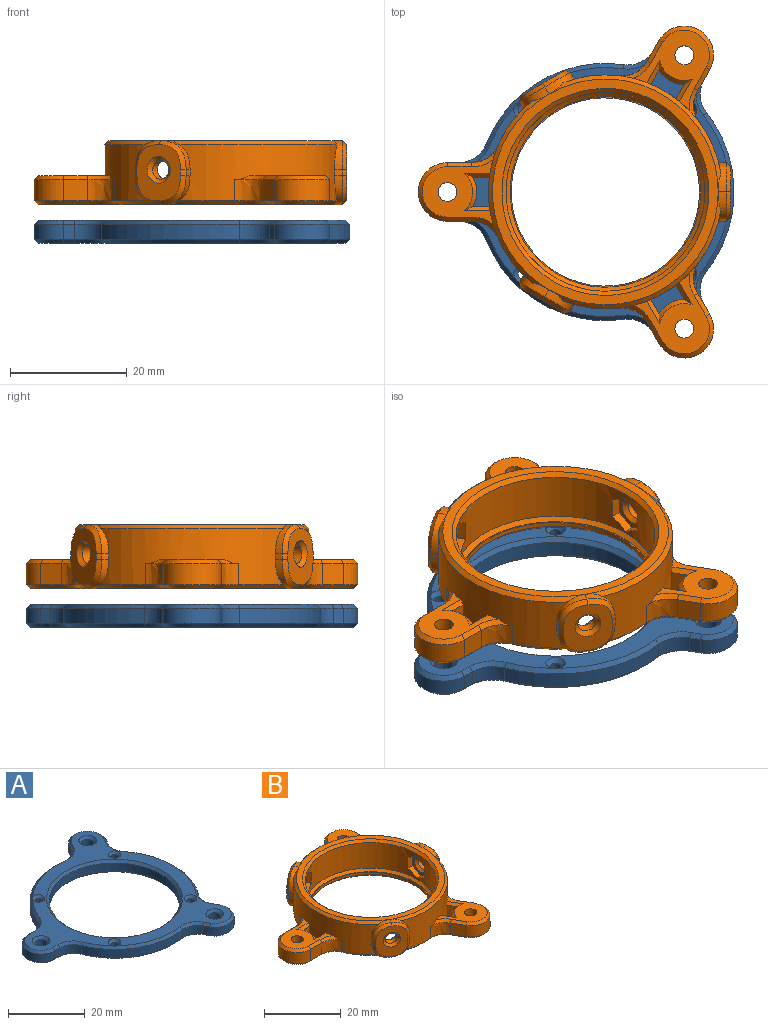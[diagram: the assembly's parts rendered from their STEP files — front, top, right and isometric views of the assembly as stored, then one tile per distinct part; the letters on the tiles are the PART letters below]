
ASSEMBLY  parts=2 mates=1
PART A: 79 faces, bbox 54x56.8x4 mm
  f0: plane 2.6x1.66mm, normal (-0.87,-0.5,0), area 5mm2, adj f1,f22,f44,f64
  f1: cylinder r=5mm len=9.33mm, axis (0,0,-1), area 40.8mm2, adj f0,f2,f46,f66
  f2: plane 2.6x1.66mm, normal (0.87,0.5,0), area 5mm2, adj f1,f23,f45,f65
  f3: cylinder r=22mm len=27.25mm, axis (0,0,-1), area 76.4mm2, adj f23,f24,f41,f61
  f4: plane 2.6x1.66mm, normal (0.87,-0.5,0), area 5mm2, adj f5,f24,f37,f56
  f5: cylinder r=5mm len=9.33mm, axis (0,0,-1), area 40.8mm2, adj f4,f6,f35,f54
  f6: plane 2.6x1.66mm, normal (-0.87,0.5,0), area 5mm2, adj f5,f25,f33,f52
  f7: cylinder r=22mm len=23.6mm, axis (0,0,-1), area 76.4mm2, adj f25,f26,f29,f48
  f8: plane 2.6x1.92mm, normal (0,1,0), area 5mm2, adj f9,f26,f32,f51
  f9: cylinder r=5mm len=10mm, axis (0,0,-1), area 40.8mm2, adj f8,f10,f34,f53
  f10: plane 2.6x1.92mm, normal (0,-1,0), area 5mm2, adj f9,f27,f36,f55
  f11: cylinder r=1.6mm len=3.2mm, axis (0,0,-1), area 26.1mm2, adj f71,f72
  f12: cylinder r=0.95mm len=3.3mm, axis (0,0,-1), area 19.7mm2, adj f21,f58
  f13: cylinder r=0.95mm len=2.6mm, axis (0,0,-1), area 15.5mm2, adj f28,f47
  f14: cylinder r=0.95mm len=2.6mm, axis (0,0,-1), area 15.5mm2, adj f68,f75
  f15: cylinder r=0.95mm len=2.6mm, axis (0,0,-1), area 15.5mm2, adj f69,f74
  f16: cylinder r=17mm len=34mm, axis (0,0,-1), area 277.7mm2, adj f77,f78
  f17: cylinder r=1.6mm len=3.2mm, axis (0,0,-1), area 26.1mm2, adj f70,f73
  f18: cylinder r=22mm len=23.6mm, axis (0,0,-1), area 76.4mm2, adj f22,f27,f40,f60
  f19: cylinder r=1.6mm len=3.2mm, axis (0,0,-1), area 26.1mm2, adj f67,f76
  f20: plane 55.37x52.6mm, normal (0,0,1), area 613.8mm2, adj f47,f48,f49,f50,f51,f52,f53,f54
  f21: plane 55.37x52.6mm, normal (0,0,-1), area 619.4mm2, adj f12,f28,f29,f30,f31,f32,f33,f34
  f22: cylinder r=5mm len=5.05mm, axis (0,0,-1), area 15.5mm2, adj f0,f18,f42,f62
  f23: cylinder r=5mm len=5.6mm, axis (0,0,-1), area 15.5mm2, adj f2,f3,f43,f63
  f24: cylinder r=5mm len=5.6mm, axis (0,0,-1), area 15.5mm2, adj f3,f4,f39,f59
  f25: cylinder r=5mm len=5.05mm, axis (0,0,-1), area 15.5mm2, adj f6,f7,f31,f50
  f26: cylinder r=5mm len=4.64mm, axis (0,0,-1), area 15.5mm2, adj f7,f8,f30,f49
  f27: cylinder r=5mm len=4.64mm, axis (0,0,-1), area 15.5mm2, adj f10,f18,f38,f57
  f28: cone r=1.65mm half-angle=45deg, axis (0,0,-1), area 8mm2, adj f13,f21,f29
  f29: cone r=22mm half-angle=45deg, axis (0,0,1), area 28.5mm2, adj f7,f21,f28,f30,f31
  f30: cone r=5.7mm half-angle=45deg, axis (0,0,-1), area 6.3mm2, adj f21,f26,f29,f32
  f31: cone r=5.7mm half-angle=45deg, axis (0,0,-1), area 6.3mm2, adj f21,f25,f29,f33
  f32: plane 1.92x0.7mm, normal (0,0.71,-0.71), area 1.9mm2, adj f8,f21,f30,f34
  f33: plane 2.01x1.57mm, normal (-0.61,0.35,-0.71), area 1.9mm2, adj f6,f21,f31,f35
  f34: cone r=5mm half-angle=45deg, axis (0,0,1), area 14.5mm2, adj f9,f21,f32,f36
  f35: cone r=5mm half-angle=45deg, axis (0,0,1), area 14.5mm2, adj f5,f21,f33,f37
  f36: plane 1.92x0.7mm, normal (0,-0.71,-0.71), area 1.9mm2, adj f10,f21,f34,f38
  f37: plane 2.01x1.57mm, normal (0.61,-0.35,-0.71), area 1.9mm2, adj f4,f21,f35,f39
  f38: cone r=5.7mm half-angle=45deg, axis (0,0,-1), area 6.3mm2, adj f21,f27,f36,f40
  f39: cone r=5.7mm half-angle=45deg, axis (0,0,-1), area 6.3mm2, adj f21,f24,f37,f41
  f40: cone r=22mm half-angle=45deg, axis (0,0,1), area 28.6mm2, adj f18,f21,f38,f42
  f41: cone r=22mm half-angle=45deg, axis (0,0,1), area 28.6mm2, adj f3,f21,f39,f43
  f42: cone r=5.7mm half-angle=45deg, axis (0,0,-1), area 6.3mm2, adj f21,f22,f40,f44
  f43: cone r=5.7mm half-angle=45deg, axis (0,0,-1), area 6.3mm2, adj f21,f23,f41,f45
  f44: plane 2.01x1.57mm, normal (-0.61,-0.35,-0.71), area 1.9mm2, adj f0,f21,f42,f46
  f45: plane 2.01x1.57mm, normal (0.61,0.35,-0.71), area 1.9mm2, adj f2,f21,f43,f46
  f46: cone r=5mm half-angle=45deg, axis (0,0,1), area 14.5mm2, adj f1,f21,f44,f45
  f47: cone r=0.95mm half-angle=45deg, axis (0,0,1), area 8mm2, adj f13,f20,f48
  f48: cone r=21.3mm half-angle=45deg, axis (0,0,-1), area 28.5mm2, adj f7,f20,f47,f49,f50
  f49: cone r=5.7mm half-angle=45deg, axis (0,0,1), area 6.3mm2, adj f20,f26,f48,f51
  f50: cone r=5.7mm half-angle=45deg, axis (0,0,1), area 6.3mm2, adj f20,f25,f48,f52
  f51: plane 1.92x0.7mm, normal (0,0.71,0.71), area 1.9mm2, adj f8,f20,f49,f53
  f52: plane 2.01x1.57mm, normal (-0.61,0.35,0.71), area 1.9mm2, adj f6,f20,f50,f54
  f53: cone r=4.3mm half-angle=45deg, axis (0,0,-1), area 14.5mm2, adj f9,f20,f51,f55
  f54: cone r=4.3mm half-angle=45deg, axis (0,0,-1), area 14.5mm2, adj f5,f20,f52,f56
  f55: plane 1.92x0.7mm, normal (0,-0.71,0.71), area 1.9mm2, adj f10,f20,f53,f57
  f56: plane 2.01x1.57mm, normal (0.61,-0.35,0.71), area 1.9mm2, adj f4,f20,f54,f59
  f57: cone r=5.7mm half-angle=45deg, axis (0,0,1), area 6.3mm2, adj f20,f27,f55,f60
  f58: cone r=0.95mm half-angle=45deg, axis (0,0,1), area 8mm2, adj f12,f20,f60
  f59: cone r=5.7mm half-angle=45deg, axis (0,0,1), area 6.3mm2, adj f20,f24,f56,f61
  f60: cone r=21.3mm half-angle=45deg, axis (0,0,-1), area 28.5mm2, adj f18,f20,f57,f58,f62
  f61: cone r=21.3mm half-angle=45deg, axis (0,0,-1), area 28.6mm2, adj f3,f20,f59,f63
  f62: cone r=5.7mm half-angle=45deg, axis (0,0,1), area 6.3mm2, adj f20,f22,f60,f64
  f63: cone r=5.7mm half-angle=45deg, axis (0,0,1), area 6.3mm2, adj f20,f23,f61,f65
  f64: plane 2.01x1.57mm, normal (-0.61,-0.35,0.71), area 1.9mm2, adj f0,f20,f62,f66
  f65: plane 2.01x1.57mm, normal (0.61,0.35,0.71), area 1.9mm2, adj f2,f20,f63,f66
  f66: cone r=4.3mm half-angle=45deg, axis (0,0,-1), area 14.5mm2, adj f1,f20,f64,f65
  f67: cone r=2.3mm half-angle=45deg, axis (0,0,-1), area 12.1mm2, adj f19,f21
  f68: cone r=1.65mm half-angle=45deg, axis (0,0,-1), area 8.1mm2, adj f14,f21
  f69: cone r=1.65mm half-angle=45deg, axis (0,0,-1), area 8.1mm2, adj f15,f21
  f70: cone r=2.3mm half-angle=45deg, axis (0,0,-1), area 12.1mm2, adj f17,f21
  f71: cone r=2.3mm half-angle=45deg, axis (0,0,-1), area 12.1mm2, adj f11,f21
  f72: cone r=1.6mm half-angle=45deg, axis (0,0,1), area 12.1mm2, adj f11,f20
  f73: cone r=1.6mm half-angle=45deg, axis (0,0,1), area 12.1mm2, adj f17,f20
  f74: cone r=0.95mm half-angle=45deg, axis (0,0,1), area 8.1mm2, adj f15,f20
  f75: cone r=0.95mm half-angle=45deg, axis (0,0,1), area 8.1mm2, adj f14,f20
  f76: cone r=1.6mm half-angle=45deg, axis (0,0,1), area 12.1mm2, adj f19,f20
  f77: cone r=17.7mm half-angle=45deg, axis (0,0,-1), area 107.9mm2, adj f16,f21
  f78: cone r=17mm half-angle=45deg, axis (0,0,1), area 107.9mm2, adj f16,f20
PART B: 173 faces, bbox 53.9x57.2x11.6 mm
  f0: cylinder r=17mm len=34mm, axis (0,0,-1), area 771.2mm2, adj f41,f42,f43,f44,f45,f46,f47,f48
  f1: plane 10x7.85mm, normal (-0.5,-0.87,0), area 54.1mm2, adj f104,f105,f106,f107,f108,f109,f149
  f2: plane 10x7.84mm, normal (-0.5,0.87,0), area 54.1mm2, adj f116,f117,f118,f119,f120,f121,f151
  f3: plane 10x9mm, normal (1,0,0), area 54.1mm2, adj f110,f111,f112,f113,f114,f115,f150
  f4: cylinder r=20mm len=27.02mm, axis (0,0,-1), area 267.1mm2, adj f9,f10,f34,f36,f38,f65,f66,f71
  f5: cylinder r=20mm len=31.2mm, axis (0,0,-1), area 267.1mm2, adj f7,f8,f24,f29,f30,f69,f70,f72
  f6: cylinder r=20mm len=27.02mm, axis (0,0,-1), area 267.1mm2, adj f11,f12,f15,f17,f22,f67,f68,f75
  f7: plane 1.18x1mm, normal (-0.87,-0.5,0), area 1.4mm2, adj f5,f79,f81,f119
  f8: plane 1.18x1mm, normal (-0.87,0.5,0), area 1.4mm2, adj f5,f72,f74,f105
  f9: plane 1.18x1mm, normal (0.87,-0.5,0), area 1.4mm2, adj f4,f71,f73,f108
  f10: plane 1.36x1mm, normal (0,-1,0), area 1.4mm2, adj f4,f76,f78,f111
  f11: plane 1.36x1mm, normal (0,1,0), area 1.4mm2, adj f6,f75,f77,f114
  f12: plane 1.18x1mm, normal (0.87,0.5,0), area 1.4mm2, adj f6,f80,f82,f118
  f13: plane 38.6x38.6mm, normal (0,0,1), area 186mm2, adj f167,f168,f169,f172
  f14: plane 55.4x50.63mm, normal (0,0,-1), area 463.6mm2, adj f83,f84,f85,f86,f87,f88,f89,f90
  f15: plane 3.6x2.45mm, normal (0.87,-0.5,0), area 10.2mm2, adj f6,f16,f145,f156
  f16: cylinder r=5mm len=4.33mm, axis (0,0,-1), area 18.8mm2, adj f15,f17,f144,f157
  f17: plane 3.6x2.45mm, normal (-0.87,0.5,0), area 10.2mm2, adj f6,f16,f143,f159
  f18: plane 3.6x3.54mm, normal (0.87,-0.5,0), area 14.7mm2, adj f19,f67,f95,f125
  f19: cylinder r=5mm len=9.33mm, axis (0,0,-1), area 56.5mm2, adj f18,f20,f97,f124
  f20: plane 3.6x3.54mm, normal (-0.87,0.5,0), area 14.7mm2, adj f19,f68,f99,f123
  f21: cylinder r=1.6mm len=4.3mm, axis (0,0,-1), area 43.2mm2, adj f22,f164
  f22: plane 14.02x13.21mm, normal (0,0,1), area 64.3mm2, adj f6,f21,f122,f123,f124,f125,f126,f143
  f23: cylinder r=5mm len=5mm, axis (0,0,-1), area 18.8mm2, adj f24,f29,f147,f155
  f24: plane 3.6x2.83mm, normal (0,-1,0), area 10.2mm2, adj f5,f23,f148,f154
  f25: plane 4.09x3.6mm, normal (0,1,0), area 14.7mm2, adj f26,f70,f98,f135
  f26: cylinder r=5mm len=10mm, axis (0,0,-1), area 56.5mm2, adj f25,f27,f96,f134
  f27: plane 4.09x3.6mm, normal (0,-1,0), area 14.7mm2, adj f26,f69,f94,f133
  f28: cylinder r=1.6mm len=4.3mm, axis (0,0,-1), area 43.2mm2, adj f30,f165
  f29: plane 3.6x2.83mm, normal (0,1,0), area 10.2mm2, adj f5,f23,f146,f153
  f30: plane 12.27x11.33mm, normal (0,0,1), area 64.3mm2, adj f5,f28,f132,f133,f134,f135,f136,f146
  f31: plane 3.6x3.54mm, normal (-0.87,-0.5,0), area 14.7mm2, adj f32,f65,f84,f130
  f32: cylinder r=5mm len=9.33mm, axis (0,0,-1), area 56.5mm2, adj f31,f33,f83,f129
  f33: plane 3.6x3.54mm, normal (0.87,0.5,0), area 14.7mm2, adj f32,f66,f85,f128
  f34: plane 3.6x2.45mm, normal (-0.87,-0.5,0), area 10.2mm2, adj f4,f35,f142,f162
  f35: cylinder r=5mm len=4.33mm, axis (0,0,-1), area 18.8mm2, adj f34,f36,f141,f160
  f36: plane 3.6x2.45mm, normal (0.87,0.5,0), area 10.2mm2, adj f4,f35,f140,f161
  f37: cylinder r=1.6mm len=4.3mm, axis (0,0,-1), area 43.2mm2, adj f38,f166
  f38: plane 14.02x13.21mm, normal (0,0,1), area 64.3mm2, adj f4,f37,f127,f128,f129,f130,f131,f140
  f39: cylinder r=16.1mm len=32.2mm, axis (0,0,-1), area 80.9mm2, adj f40,f170
  f40: plane 32.6x32.6mm, normal (0,0,1), area 20.4mm2, adj f39,f171
  f41: plane 3.01x1.74mm, normal (0,-0.5,0.87), area 5.2mm2, adj f0,f42,f46,f60
  f42: plane 3.46x1.69mm, normal (0,-1,0), area 5.9mm2, adj f0,f41,f43,f60
  f43: plane 3.01x1.74mm, normal (0,-0.5,-0.87), area 5.2mm2, adj f0,f42,f44,f60
  f44: plane 3.01x1.74mm, normal (0,0.5,-0.87), area 5.2mm2, adj f0,f43,f45,f60
  f45: plane 3.46x1.69mm, normal (0,1,0), area 5.9mm2, adj f0,f44,f46,f60
  f46: plane 3.01x1.74mm, normal (0,0.5,0.87), area 5.2mm2, adj f0,f41,f45,f60
  f47: plane 3.32x2.97mm, normal (0.43,0.25,0.87), area 5.2mm2, adj f0,f48,f52,f62
  f48: plane 3.46x1.46mm, normal (0.87,0.5,0), area 5.9mm2, adj f0,f47,f49,f62
  f49: plane 3.32x2.97mm, normal (0.43,0.25,-0.87), area 5.2mm2, adj f0,f48,f50,f62
  f50: plane 3.45x2.74mm, normal (-0.43,-0.25,-0.87), area 5.2mm2, adj f0,f49,f51,f62
  f51: plane 3.46x1.46mm, normal (-0.87,-0.5,0), area 5.9mm2, adj f0,f50,f52,f62
  f52: plane 3.45x2.74mm, normal (-0.43,-0.25,0.87), area 5.2mm2, adj f0,f47,f51,f62
  f53: plane 3.45x2.74mm, normal (-0.43,0.25,0.87), area 5.2mm2, adj f0,f54,f58,f64
  f54: plane 3.46x1.46mm, normal (-0.87,0.5,0), area 5.9mm2, adj f0,f53,f55,f64
  f55: plane 3.45x2.74mm, normal (-0.43,0.25,-0.87), area 5.2mm2, adj f0,f54,f56,f64
  f56: plane 3.32x2.97mm, normal (0.43,-0.25,-0.87), area 5.2mm2, adj f0,f55,f57,f64
  f57: plane 3.46x1.46mm, normal (0.87,-0.5,0), area 5.9mm2, adj f0,f56,f58,f64
  f58: plane 3.32x2.97mm, normal (0.43,-0.25,0.87), area 5.2mm2, adj f0,f53,f57,f64
  f59: cylinder r=1.6mm len=3.2mm, axis (1,0,0), area 16.1mm2, adj f138,f150
  f60: plane 6.93x6mm, normal (-1,0,0), area 14.6mm2, adj f41,f42,f43,f44,f45,f46,f138
  f61: cylinder r=1.6mm len=3.57mm, axis (-0.5,0.87,0), area 16.1mm2, adj f139,f151
  f62: plane 6.93x5.2mm, normal (0.5,-0.87,0), area 14.6mm2, adj f47,f48,f49,f50,f51,f52,f139
  f63: cylinder r=1.6mm len=3.57mm, axis (-0.5,-0.87,0), area 16.1mm2, adj f137,f149
  f64: plane 6.93x5.2mm, normal (0.5,0.87,0), area 14.6mm2, adj f53,f54,f55,f56,f57,f58,f137
  f65: bspline ~5.5x4.89mm, area 21mm2, adj f4,f31,f86,f131
  f66: bspline ~5.5x5.47mm, area 21mm2, adj f4,f33,f87,f127
  f67: bspline ~5.5x5.47mm, area 21mm2, adj f6,f18,f93,f126
  f68: bspline ~5.5x4.89mm, area 21mm2, adj f6,f20,f101,f122
  f69: bspline ~5.5x4.58mm, area 21mm2, adj f5,f27,f92,f132
  f70: bspline ~5.5x4.58mm, area 21mm2, adj f5,f25,f100,f136
  f71: bspline ~5.04x5mm, area 9.6mm2, adj f4,f9,f72,f106,f167
  f72: bspline ~5.46x5mm, area 9.6mm2, adj f5,f8,f71,f104,f168
  f73: bspline ~5.04x5mm, area 9.6mm2, adj f4,f9,f74,f88,f109
  f74: bspline ~5.46x5mm, area 9.6mm2, adj f5,f8,f73,f90,f107
  f75: bspline ~5x5mm, area 9.6mm2, adj f6,f11,f76,f112,f169
  f76: bspline ~5x5mm, area 9.6mm2, adj f4,f10,f75,f110,f167
  f77: bspline ~5x5mm, area 9.6mm2, adj f6,f11,f78,f91,f115
  f78: bspline ~5x5mm, area 9.6mm2, adj f4,f10,f77,f89,f113
  f79: bspline ~5.46x5mm, area 9.6mm2, adj f5,f7,f80,f121,f168
  f80: bspline ~5.04x5mm, area 9.6mm2, adj f6,f12,f79,f120,f169
  f81: bspline ~5.46x5mm, area 9.6mm2, adj f5,f7,f82,f102,f117
  f82: bspline ~5.04x5mm, area 9.6mm2, adj f6,f12,f81,f103,f116
  f83: cone r=5mm half-angle=45deg, axis (0,0,1), area 14.5mm2, adj f14,f32,f84,f85
  f84: plane 3.89x2.65mm, normal (-0.61,-0.35,-0.71), area 4mm2, adj f14,f31,f83,f86
  f85: plane 3.89x2.65mm, normal (0.61,0.35,-0.71), area 4mm2, adj f14,f33,f83,f87
  f86: bspline ~5.57x3.29mm, area 6.2mm2, adj f14,f65,f84,f88
  f87: bspline ~6.23x1.81mm, area 6.2mm2, adj f14,f66,f85,f89
  f88: cone r=20mm half-angle=45deg, axis (0,0,1), area 10.9mm2, adj f4,f14,f73,f86
  f89: cone r=20mm half-angle=45deg, axis (0,0,1), area 10.9mm2, adj f4,f14,f78,f87
  f90: cone r=20mm half-angle=45deg, axis (0,0,1), area 10.9mm2, adj f5,f14,f74,f92
  f91: cone r=20mm half-angle=45deg, axis (0,0,1), area 10.9mm2, adj f6,f14,f77,f93
  f92: bspline ~5.22x3.7mm, area 6.2mm2, adj f14,f69,f90,f94
  f93: bspline ~6.23x1.81mm, area 6.2mm2, adj f14,f67,f91,f95
  f94: plane 4.09x0.7mm, normal (0,-0.71,-0.71), area 4mm2, adj f14,f27,f92,f96
  f95: plane 3.89x2.65mm, normal (0.61,-0.35,-0.71), area 4mm2, adj f14,f18,f93,f97
  f96: cone r=5mm half-angle=45deg, axis (0,0,1), area 14.5mm2, adj f14,f26,f94,f98
  f97: cone r=5mm half-angle=45deg, axis (0,0,1), area 14.5mm2, adj f14,f19,f95,f99
  f98: plane 4.09x0.7mm, normal (0,0.71,-0.71), area 4mm2, adj f14,f25,f96,f100
  f99: plane 3.89x2.65mm, normal (-0.61,0.35,-0.71), area 4mm2, adj f14,f20,f97,f101
  f100: bspline ~5.22x3.71mm, area 6.2mm2, adj f14,f70,f98,f102
  f101: bspline ~5.57x3.29mm, area 6.2mm2, adj f14,f68,f99,f103
  f102: cone r=20mm half-angle=45deg, axis (0,0,1), area 10.9mm2, adj f5,f14,f81,f100
  f103: cone r=20mm half-angle=45deg, axis (0,0,1), area 10.9mm2, adj f6,f14,f82,f101
  f104: bspline ~5x4.33mm, area 7.5mm2, adj f1,f72,f105,f106
  f105: plane 1x0.96mm, normal (-0.97,-0.26,0), area 1mm2, adj f1,f8,f104,f107
  f106: bspline ~5x4.68mm, area 7.5mm2, adj f1,f71,f104,f108
  f107: bspline ~5x4.33mm, area 7.5mm2, adj f1,f74,f105,f109
  f108: plane 1x0.96mm, normal (0.26,-0.97,0), area 1mm2, adj f1,f9,f106,f109
  f109: bspline ~5x4.68mm, area 7.5mm2, adj f1,f73,f107,f108
  f110: bspline ~5x5mm, area 7.5mm2, adj f3,f76,f111,f112
  f111: plane 1x0.7mm, normal (0.71,-0.71,0), area 1mm2, adj f3,f10,f110,f113
  f112: bspline ~5x5mm, area 7.5mm2, adj f3,f75,f110,f114
  f113: bspline ~5x5mm, area 7.5mm2, adj f3,f78,f111,f115
  f114: plane 1x0.7mm, normal (0.71,0.71,0), area 1mm2, adj f3,f11,f112,f115
  f115: bspline ~5x5mm, area 7.5mm2, adj f3,f77,f113,f114
  f116: bspline ~5x4.68mm, area 7.5mm2, adj f2,f82,f117,f118
  f117: bspline ~5x4.33mm, area 7.5mm2, adj f2,f81,f116,f119
  f118: plane 1x0.96mm, normal (0.26,0.97,0), area 1mm2, adj f2,f12,f116,f120
  f119: plane 1x0.96mm, normal (-0.97,0.26,0), area 1mm2, adj f2,f7,f117,f121
  f120: bspline ~5x4.68mm, area 7.5mm2, adj f2,f80,f118,f121
  f121: bspline ~5x4.33mm, area 7.5mm2, adj f2,f79,f119,f120
  f122: bspline ~5.57x3.21mm, area 4.9mm2, adj f6,f22,f68,f123
  f123: plane 3.89x2.65mm, normal (-0.61,0.35,0.71), area 4mm2, adj f20,f22,f122,f124
  f124: cone r=4.3mm half-angle=45deg, axis (0,0,-1), area 14.5mm2, adj f19,f22,f123,f125
  f125: plane 3.89x2.65mm, normal (0.61,-0.35,0.71), area 4mm2, adj f18,f22,f124,f126
  f126: bspline ~6.23x1.76mm, area 4.9mm2, adj f6,f22,f67,f125
  f127: bspline ~6.23x1.76mm, area 4.9mm2, adj f4,f38,f66,f128
  f128: plane 3.89x2.65mm, normal (0.61,0.35,0.71), area 4mm2, adj f33,f38,f127,f129
  f129: cone r=4.3mm half-angle=45deg, axis (0,0,-1), area 14.5mm2, adj f32,f38,f128,f130
  f130: plane 3.89x2.65mm, normal (-0.61,-0.35,0.71), area 4mm2, adj f31,f38,f129,f131
  f131: bspline ~5.91x3.22mm, area 4.9mm2, adj f4,f38,f65,f130
  f132: bspline ~5.36x4.01mm, area 4.9mm2, adj f5,f30,f69,f133
  f133: plane 4.09x0.7mm, normal (0,-0.71,0.71), area 4mm2, adj f27,f30,f132,f134
  f134: cone r=4.3mm half-angle=45deg, axis (0,0,-1), area 14.5mm2, adj f26,f30,f133,f135
  f135: plane 4.09x0.7mm, normal (0,0.71,0.71), area 4mm2, adj f25,f30,f134,f136
  f136: bspline ~5.36x4.01mm, area 4.9mm2, adj f5,f30,f70,f135
  f137: cone r=2.3mm half-angle=45deg, axis (0.5,0.87,0), area 12.1mm2, adj f63,f64
  f138: cone r=2.3mm half-angle=45deg, axis (-1,0,0), area 12.1mm2, adj f59,f60
  f139: cone r=2.3mm half-angle=45deg, axis (0.5,-0.87,0), area 12.1mm2, adj f61,f62
  f140: plane 4.18x2.32mm, normal (0.61,0.35,0.71), area 3.5mm2, adj f4,f36,f38,f141
  f141: cone r=4.3mm half-angle=45deg, axis (0,0,-1), area 6.2mm2, adj f35,f38,f140,f142
  f142: plane 3.92x2.87mm, normal (-0.61,-0.35,0.71), area 3.5mm2, adj f4,f34,f38,f141
  f143: plane 3.92x2.87mm, normal (-0.61,0.35,0.71), area 3.5mm2, adj f6,f17,f22,f144
  f144: cone r=4.3mm half-angle=45deg, axis (0,0,-1), area 6.2mm2, adj f16,f22,f143,f145
  f145: plane 4.18x2.32mm, normal (0.61,-0.35,0.71), area 3.5mm2, adj f6,f15,f22,f144
  f146: plane 4.51x0.82mm, normal (0,0.71,0.71), area 3.5mm2, adj f5,f29,f30,f147
  f147: cone r=4.3mm half-angle=45deg, axis (0,0,-1), area 6.2mm2, adj f23,f30,f146,f148
  f148: plane 4.51x0.82mm, normal (0,-0.71,0.71), area 3.5mm2, adj f5,f24,f30,f147
  f149: cone r=1.6mm half-angle=45deg, axis (-0.5,-0.87,0), area 12.1mm2, adj f1,f63
  f150: cone r=1.6mm half-angle=45deg, axis (1,0,0), area 12.1mm2, adj f3,f59
  f151: cone r=1.6mm half-angle=45deg, axis (-0.5,0.87,0), area 12.1mm2, adj f2,f61
  f152: cone r=20mm half-angle=45deg, axis (0,0,1), area 5.7mm2, adj f5,f14,f153,f154
  f153: plane 5.22x0.82mm, normal (0,0.71,-0.71), area 3.9mm2, adj f14,f29,f152,f155
  f154: plane 5.22x0.82mm, normal (0,-0.71,-0.71), area 3.9mm2, adj f14,f24,f152,f155
  f155: cone r=5mm half-angle=45deg, axis (0,0,1), area 6.2mm2, adj f14,f23,f153,f154
  f156: plane 4.54x2.67mm, normal (0.61,-0.35,-0.71), area 3.9mm2, adj f14,f15,f157,f158
  f157: cone r=5mm half-angle=45deg, axis (0,0,1), area 6.2mm2, adj f14,f16,f156,f159
  f158: cone r=20mm half-angle=45deg, axis (0,0,1), area 5.7mm2, adj f6,f14,f156,f159
  f159: plane 4.54x2.87mm, normal (-0.61,0.35,-0.71), area 3.9mm2, adj f14,f17,f157,f158
  f160: cone r=5mm half-angle=45deg, axis (0,0,1), area 6.2mm2, adj f14,f35,f161,f162
  f161: plane 4.54x2.67mm, normal (0.61,0.35,-0.71), area 3.9mm2, adj f14,f36,f160,f163
  f162: plane 4.54x2.87mm, normal (-0.61,-0.35,-0.71), area 3.9mm2, adj f14,f34,f160,f163
  f163: cone r=20mm half-angle=45deg, axis (0,0,1), area 5.7mm2, adj f4,f14,f161,f162
  f164: cone r=2.3mm half-angle=45deg, axis (0,0,-1), area 12.1mm2, adj f14,f21
  f165: cone r=2.3mm half-angle=45deg, axis (0,0,-1), area 12.1mm2, adj f14,f28
  f166: cone r=2.3mm half-angle=45deg, axis (0,0,-1), area 12.1mm2, adj f14,f37
  f167: cone r=19.3mm half-angle=45deg, axis (0,0,-1), area 37.7mm2, adj f4,f13,f71,f76
  f168: cone r=19.3mm half-angle=45deg, axis (0,0,-1), area 37.7mm2, adj f5,f13,f72,f79
  f169: cone r=19.3mm half-angle=45deg, axis (0,0,-1), area 37.7mm2, adj f6,f13,f75,f80
  f170: cone r=16.8mm half-angle=45deg, axis (0,0,-1), area 102.3mm2, adj f14,f39
  f171: cone r=16.3mm half-angle=45deg, axis (0,0,1), area 103.6mm2, adj f0,f40
  f172: cone r=17mm half-angle=45deg, axis (0,0,1), area 107.9mm2, adj f0,f13
PLACE A t=(-2.52,-11.77,9.39)mm
PLACE B t=(0.35,-8.47,15.99)mm
MATE slider B.f23 <-> A.f9  axis (0,0,1) through (-26.65,-8.47,16.69)mm
